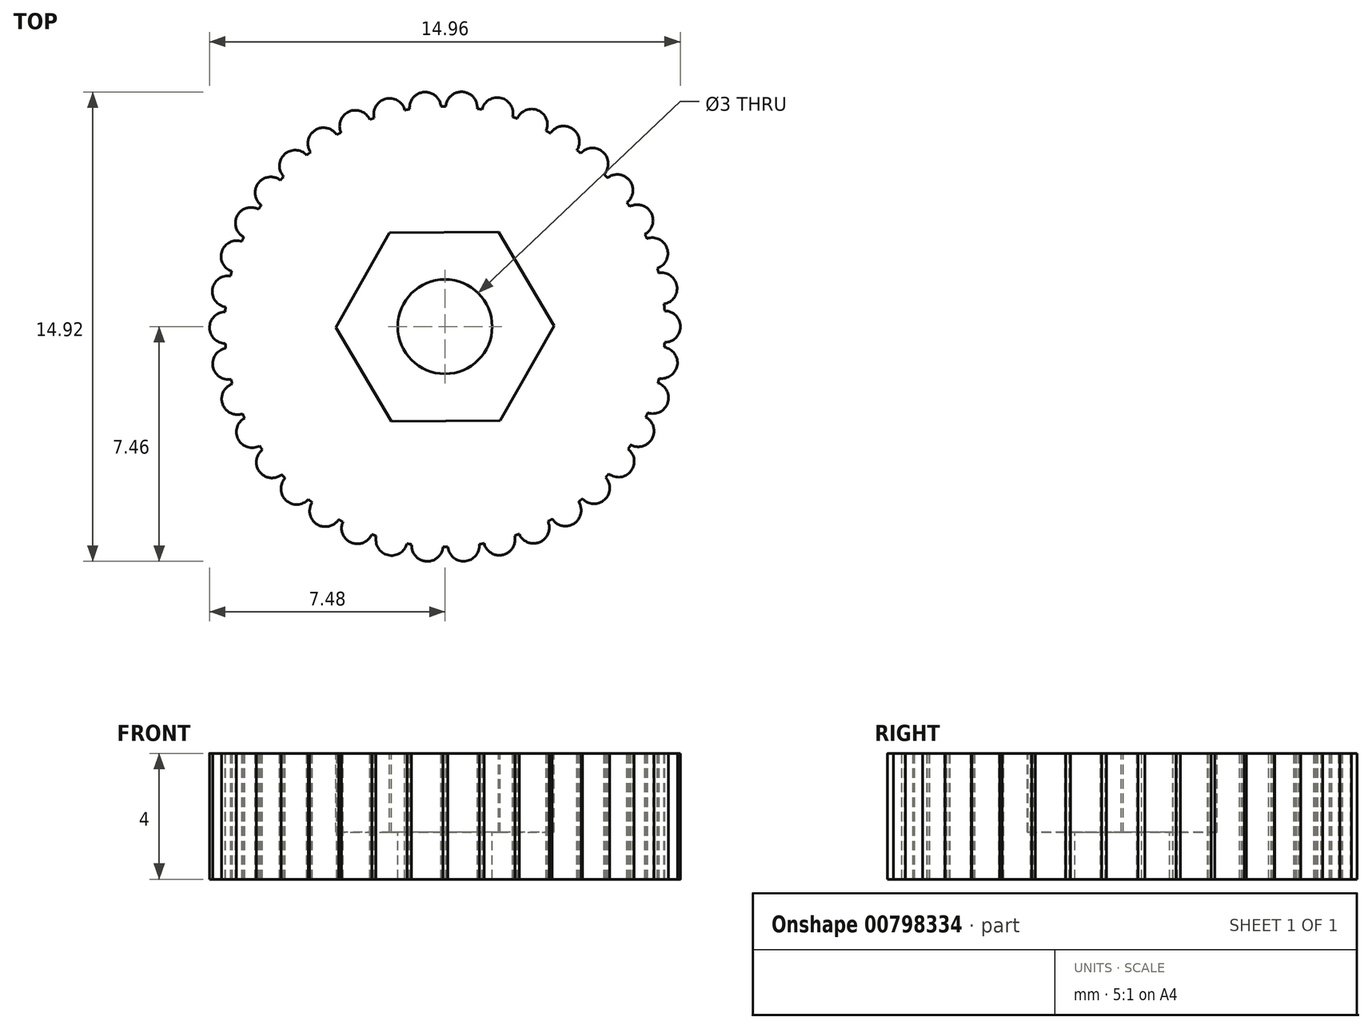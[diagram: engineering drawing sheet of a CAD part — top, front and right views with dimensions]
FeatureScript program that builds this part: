
annotation { "Feature Type Name" : "Feature", "Feature Type Description" : "" }
export const myFeature = defineFeature(function(context is Context, id is Id, definition is map)
    precondition{}
    {
        {
            var Q0;
            Q0=qCreatedBy(makeId("Top.planeOp"),FACE);
            var sketch = newSketch(context, id + "F0", { "sketchPlane" : qUnion([Q0])});
            skCircle(sketch, "E0", {"center": v(0, 0) * mm, "radius": 7 * mm});
            skCircle(sketch, "E1.cCircle", {"center": v(0, 0) * mm, "radius": 3 * mm, "construction": true});
            skLineSegment(sketch, "E1.0", {"start": v(3.46, 0.03) * mm, "end": v(1.76, -2.98) * mm});
            skLineSegment(sketch, "E1.1", {"start": v(1.76, -2.98) * mm, "end": v(-1.7, -3.02) * mm});
            skLineSegment(sketch, "E1.2", {"start": v(-1.7, -3.02) * mm, "end": v(-3.46, -0.03) * mm});
            skLineSegment(sketch, "E1.3", {"start": v(-3.46, -0.03) * mm, "end": v(-1.76, 2.98) * mm});
            skLineSegment(sketch, "E1.4", {"start": v(-1.76, 2.98) * mm, "end": v(1.7, 3.02) * mm});
            skLineSegment(sketch, "E1.5", {"start": v(1.7, 3.02) * mm, "end": v(3.46, 0.03) * mm});
            skPoint(sketch, "E1.0.midPoint", {"position": v(2.61, -1.48) * mm});
            skCircle(sketch, "E2", {"center": v(0, 0) * mm, "radius": 1.5 * mm});
            skLineSegment(sketch, "E3", {"start": v(6.4, 0) * mm, "end": v(8.22, 0) * mm, "construction": true});
            skArc(sketch, "E4", {"start": v(6.98, -0.5) * mm, "mid": v(7.48, 0) * mm, "end": v(6.98, 0.5) * mm});
            skArc(sketch, "E5.1.0", {"start": v(6.8, -1.64) * mm, "mid": v(7.38, -1.23) * mm, "end": v(6.97, -0.65) * mm});
            skArc(sketch, "E5.2.0", {"start": v(6.44, -2.74) * mm, "mid": v(7.08, -2.43) * mm, "end": v(6.77, -1.8) * mm});
            skArc(sketch, "E5.3.0", {"start": v(5.9, -3.76) * mm, "mid": v(6.58, -3.56) * mm, "end": v(6.38, -2.88) * mm});
            skArc(sketch, "E5.4.0", {"start": v(5.2, -4.68) * mm, "mid": v(5.9, -4.59) * mm, "end": v(5.82, -3.89) * mm});
            skArc(sketch, "E5.5.0", {"start": v(4.37, -5.47) * mm, "mid": v(5.07, -5.5) * mm, "end": v(5.1, -4.8) * mm});
            skArc(sketch, "E5.6.0", {"start": v(3.4, -6.11) * mm, "mid": v(4.1, -6.26) * mm, "end": v(4.25, -5.57) * mm});
            skArc(sketch, "E5.7.0", {"start": v(2.36, -6.6) * mm, "mid": v(3.02, -6.85) * mm, "end": v(3.27, -6.19) * mm});
            skArc(sketch, "E5.8.0", {"start": v(1.24, -6.89) * mm, "mid": v(1.85, -7.25) * mm, "end": v(2.21, -6.64) * mm});
            skArc(sketch, "E5.9.0", {"start": v(0.1, -7) * mm, "mid": v(0.63, -7.46) * mm, "end": v(1.1, -6.91) * mm});
            skArc(sketch, "E5.10.0", {"start": v(-1.06, -6.92) * mm, "mid": v(-0.6, -7.46) * mm, "end": v(-0.06, -7) * mm});
            skArc(sketch, "E5.11.0", {"start": v(-2.18, -6.65) * mm, "mid": v(-1.82, -7.26) * mm, "end": v(-1.21, -6.9) * mm});
            skArc(sketch, "E5.12.0", {"start": v(-3.24, -6.2) * mm, "mid": v(-2.99, -6.86) * mm, "end": v(-2.33, -6.6) * mm});
            skArc(sketch, "E5.13.0", {"start": v(-4.22, -5.59) * mm, "mid": v(-4.07, -6.28) * mm, "end": v(-3.38, -6.13) * mm});
            skArc(sketch, "E5.14.0", {"start": v(-5.08, -4.82) * mm, "mid": v(-5.05, -5.52) * mm, "end": v(-4.34, -5.5) * mm});
            skArc(sketch, "E5.15.0", {"start": v(-5.8, -3.92) * mm, "mid": v(-5.89, -4.62) * mm, "end": v(-5.19, -4.7) * mm});
            skArc(sketch, "E5.16.0", {"start": v(-6.37, -2.9) * mm, "mid": v(-6.57, -3.59) * mm, "end": v(-5.89, -3.79) * mm});
            skArc(sketch, "E5.17.0", {"start": v(-6.76, -1.82) * mm, "mid": v(-7.07, -2.46) * mm, "end": v(-6.43, -2.77) * mm});
            skArc(sketch, "E5.18.0", {"start": v(-6.97, -0.69) * mm, "mid": v(-7.37, -1.26) * mm, "end": v(-6.8, -1.67) * mm});
            skArc(sketch, "E5.19.0", {"start": v(-6.98, 0.47) * mm, "mid": v(-7.48, -0.04) * mm, "end": v(-6.98, -0.53) * mm});
            skArc(sketch, "E5.20.0", {"start": v(-6.81, 1.6) * mm, "mid": v(-7.39, 1.2) * mm, "end": v(-6.97, 0.62) * mm});
            skArc(sketch, "E5.21.0", {"start": v(-6.46, 2.7) * mm, "mid": v(-7.09, 2.4) * mm, "end": v(-6.78, 1.76) * mm});
            skArc(sketch, "E5.22.0", {"start": v(-5.92, 3.73) * mm, "mid": v(-6.6, 3.53) * mm, "end": v(-6.4, 2.85) * mm});
            skArc(sketch, "E5.23.0", {"start": v(-5.23, 4.65) * mm, "mid": v(-5.93, 4.56) * mm, "end": v(-5.84, 3.86) * mm});
            skArc(sketch, "E5.24.0", {"start": v(-4.4, 5.45) * mm, "mid": v(-5.1, 5.47) * mm, "end": v(-5.13, 4.77) * mm});
            skArc(sketch, "E5.25.0", {"start": v(-3.44, 6.1) * mm, "mid": v(-4.13, 6.24) * mm, "end": v(-4.27, 5.55) * mm});
            skArc(sketch, "E5.26.0", {"start": v(-2.39, 6.58) * mm, "mid": v(-3.05, 6.83) * mm, "end": v(-3.3, 6.17) * mm});
            skArc(sketch, "E5.27.0", {"start": v(-1.28, 6.88) * mm, "mid": v(-1.89, 7.24) * mm, "end": v(-2.24, 6.63) * mm});
            skArc(sketch, "E5.28.0", {"start": v(-0.13, 7) * mm, "mid": v(-0.67, 7.45) * mm, "end": v(-1.12, 6.9) * mm});
            skArc(sketch, "E5.29.0", {"start": v(1.03, 6.92) * mm, "mid": v(0.56, 7.46) * mm, "end": v(0.03, 7) * mm});
            skArc(sketch, "E5.30.0", {"start": v(2.15, 6.66) * mm, "mid": v(1.78, 7.27) * mm, "end": v(1.18, 6.9) * mm});
            skArc(sketch, "E5.31.0", {"start": v(3.21, 6.22) * mm, "mid": v(2.95, 6.87) * mm, "end": v(2.3, 6.61) * mm});
            skArc(sketch, "E5.32.0", {"start": v(4.2, 5.6) * mm, "mid": v(4.04, 6.3) * mm, "end": v(3.35, 6.15) * mm});
            skArc(sketch, "E5.33.0", {"start": v(5.06, 4.84) * mm, "mid": v(5.02, 5.55) * mm, "end": v(4.32, 5.51) * mm});
            skArc(sketch, "E5.34.0", {"start": v(5.78, 3.94) * mm, "mid": v(5.87, 4.65) * mm, "end": v(5.16, 4.73) * mm});
            skLineSegment(sketch, "E5.anchor1", {"start": v(0, 0) * mm, "end": v(6.98, -0.5) * mm, "construction": true});
            skLineSegment(sketch, "E5.anchor2", {"start": v(0, 0) * mm, "end": v(6.96, 0.72) * mm, "construction": true});
            skArc(sketch, "E6.2.35.0", {"start": v(6.35, 2.94) * mm, "mid": v(6.55, 3.62) * mm, "end": v(5.87, 3.81) * mm});
            skArc(sketch, "E7.2.36.0", {"start": v(6.75, 1.85) * mm, "mid": v(7.05, 2.5) * mm, "end": v(6.42, 2.8) * mm});
            skArc(sketch, "E7.2.37.0", {"start": v(6.96, 0.72) * mm, "mid": v(7.37, 1.3) * mm, "end": v(6.79, 1.7) * mm});
            skSolve(sketch);
        }
        {
            var Q0;
            Q0 = qSketchRegion(id + "F0", true);
            var Q1;
            Q1=makeQuery(id+"F0.imprint","IMPRINT",FACE,{"disambiguationData":[TD([[makeQuery(id+"F0.imprint","IMPRINT",EDGE,{"derivedFrom":sQuery(id+"F0.wireOp",EDGE,"E1.0")}),-1.0]])]});
            extrude(context, id + "F1", {"entities" : qUnion([Q0, Q1]), "depth" : 4 * mm, "offsetDistance" : 25 * mm});
        }
        {
            var Q0;
            Q0=makeQuery(id+"F0.imprint","IMPRINT",FACE,{"disambiguationData":[TD([[makeQuery(id+"F0.imprint","IMPRINT",EDGE,{"derivedFrom":sQuery(id+"F0.wireOp",EDGE,"E1.0")}),-1.0]])]});
            extrude(context, id + "F2", {"entities" : qUnion([Q0]), "operationType" : NewBodyOperationType.REMOVE, "depth" : 2.5 * mm, "offsetDistance" : 25 * mm});
        }
        {
            var Q0;
            Q0=makeQuery(id+"F1.opExtrude","SWEPT_BODY",BODY,{"disambiguationData":[OSD([sQuery(id+"F0.wireOp",EDGE,"E0"),sQuery(id+"F0.wireOp",EDGE,"E2"),sQuery(id+"F0.wireOp",EDGE,"E4"),sQuery(id+"F0.wireOp",EDGE,"E5.1.0"),sQuery(id+"F0.wireOp",EDGE,"E5.2.0"),sQuery(id+"F0.wireOp",EDGE,"E5.3.0"),sQuery(id+"F0.wireOp",EDGE,"E5.4.0"),sQuery(id+"F0.wireOp",EDGE,"E5.5.0"),sQuery(id+"F0.wireOp",EDGE,"E5.6.0"),sQuery(id+"F0.wireOp",EDGE,"E5.7.0"),sQuery(id+"F0.wireOp",EDGE,"E5.8.0"),sQuery(id+"F0.wireOp",EDGE,"E5.9.0"),sQuery(id+"F0.wireOp",EDGE,"E5.10.0"),sQuery(id+"F0.wireOp",EDGE,"E5.11.0"),sQuery(id+"F0.wireOp",EDGE,"E5.12.0"),sQuery(id+"F0.wireOp",EDGE,"E5.13.0"),sQuery(id+"F0.wireOp",EDGE,"E5.14.0"),sQuery(id+"F0.wireOp",EDGE,"E5.15.0"),sQuery(id+"F0.wireOp",EDGE,"E5.16.0"),sQuery(id+"F0.wireOp",EDGE,"E5.17.0"),sQuery(id+"F0.wireOp",EDGE,"E5.18.0"),sQuery(id+"F0.wireOp",EDGE,"E5.19.0"),sQuery(id+"F0.wireOp",EDGE,"E5.20.0"),sQuery(id+"F0.wireOp",EDGE,"E5.21.0"),sQuery(id+"F0.wireOp",EDGE,"E5.22.0"),sQuery(id+"F0.wireOp",EDGE,"E5.23.0"),sQuery(id+"F0.wireOp",EDGE,"E5.24.0"),sQuery(id+"F0.wireOp",EDGE,"E5.25.0"),sQuery(id+"F0.wireOp",EDGE,"E5.26.0"),sQuery(id+"F0.wireOp",EDGE,"E5.27.0"),sQuery(id+"F0.wireOp",EDGE,"E5.28.0"),sQuery(id+"F0.wireOp",EDGE,"E5.29.0"),sQuery(id+"F0.wireOp",EDGE,"E5.30.0"),sQuery(id+"F0.wireOp",EDGE,"E5.31.0"),sQuery(id+"F0.wireOp",EDGE,"E5.32.0"),sQuery(id+"F0.wireOp",EDGE,"E5.33.0"),sQuery(id+"F0.wireOp",EDGE,"E5.34.0"),sQuery(id+"F0.wireOp",EDGE,"E6.2.35.0"),sQuery(id+"F0.wireOp",EDGE,"E7.2.36.0"),sQuery(id+"F0.wireOp",EDGE,"E7.2.37.0")])]});
            var Q1;
            Q1=qCreatedBy(makeId("Top.planeOp"),FACE);
            mirror(context, id + "F3", {"entities" : qUnion([Q0]), "mirrorPlane" : qUnion([Q1])});
        }
        {
            var Q0;
            Q0=makeQuery(id+"F1.opExtrude","SWEPT_BODY",BODY,{"disambiguationData":[OSD([sQuery(id+"F0.wireOp",EDGE,"E0"),sQuery(id+"F0.wireOp",EDGE,"E2"),sQuery(id+"F0.wireOp",EDGE,"E4"),sQuery(id+"F0.wireOp",EDGE,"E5.1.0"),sQuery(id+"F0.wireOp",EDGE,"E5.2.0"),sQuery(id+"F0.wireOp",EDGE,"E5.3.0"),sQuery(id+"F0.wireOp",EDGE,"E5.4.0"),sQuery(id+"F0.wireOp",EDGE,"E5.5.0"),sQuery(id+"F0.wireOp",EDGE,"E5.6.0"),sQuery(id+"F0.wireOp",EDGE,"E5.7.0"),sQuery(id+"F0.wireOp",EDGE,"E5.8.0"),sQuery(id+"F0.wireOp",EDGE,"E5.9.0"),sQuery(id+"F0.wireOp",EDGE,"E5.10.0"),sQuery(id+"F0.wireOp",EDGE,"E5.11.0"),sQuery(id+"F0.wireOp",EDGE,"E5.12.0"),sQuery(id+"F0.wireOp",EDGE,"E5.13.0"),sQuery(id+"F0.wireOp",EDGE,"E5.14.0"),sQuery(id+"F0.wireOp",EDGE,"E5.15.0"),sQuery(id+"F0.wireOp",EDGE,"E5.16.0"),sQuery(id+"F0.wireOp",EDGE,"E5.17.0"),sQuery(id+"F0.wireOp",EDGE,"E5.18.0"),sQuery(id+"F0.wireOp",EDGE,"E5.19.0"),sQuery(id+"F0.wireOp",EDGE,"E5.20.0"),sQuery(id+"F0.wireOp",EDGE,"E5.21.0"),sQuery(id+"F0.wireOp",EDGE,"E5.22.0"),sQuery(id+"F0.wireOp",EDGE,"E5.23.0"),sQuery(id+"F0.wireOp",EDGE,"E5.24.0"),sQuery(id+"F0.wireOp",EDGE,"E5.25.0"),sQuery(id+"F0.wireOp",EDGE,"E5.26.0"),sQuery(id+"F0.wireOp",EDGE,"E5.27.0"),sQuery(id+"F0.wireOp",EDGE,"E5.28.0"),sQuery(id+"F0.wireOp",EDGE,"E5.29.0"),sQuery(id+"F0.wireOp",EDGE,"E5.30.0"),sQuery(id+"F0.wireOp",EDGE,"E5.31.0"),sQuery(id+"F0.wireOp",EDGE,"E5.32.0"),sQuery(id+"F0.wireOp",EDGE,"E5.33.0"),sQuery(id+"F0.wireOp",EDGE,"E5.34.0"),sQuery(id+"F0.wireOp",EDGE,"E6.2.35.0"),sQuery(id+"F0.wireOp",EDGE,"E7.2.36.0"),sQuery(id+"F0.wireOp",EDGE,"E7.2.37.0")])]});
            deleteBodies(context, id + "F4", {"entities" : qUnion([Q0])});
        }
    });
